# Revit family: Trim_Casing
name_source: partatom
category: Generic Models
units: mm (PartAtom-declared; Revit-internal decimal feet)

## family parameters
Can host rebar = No
Classification Number = 23.35.10.34.17
Cut with Voids When Loaded = No
Maintain Annotation Orientation = No
Part Type = Normal
Room Calculation Point = No
Round Connector Dimension = Use Diameter
Shared = No

## types (1)
- ByProfile
    Assembly Code = C3010130
    Construction Details = http://www.arcat.com
    Default Elevation = 0' - 0"
    Description = Window and Door Casing
    Expected Lifespan (Years) = 30
    Green Building-LEED = http://www.arcat.com
    Keynote = 06450
    Maintenance Schedule (Months) = 12
    Manufacturer = Generic
    Manufacturer Fax = (203) 929-2444
    Manufacturer Website = http://www.arcat.com
    Model = Generic
    Product Data = http://www.arcat.com
    Product Properties = http://www.arcat.com
    Specification = http://www.arcat.com
    Trim Material = ARCAT - Wood - Pine_FJ-Primed
    Warranty Duration (Years) = 1

## geometry (parser evidence)
native form markers: Blend x3, Sweep x12
no freeform markers — native parametric forms only
